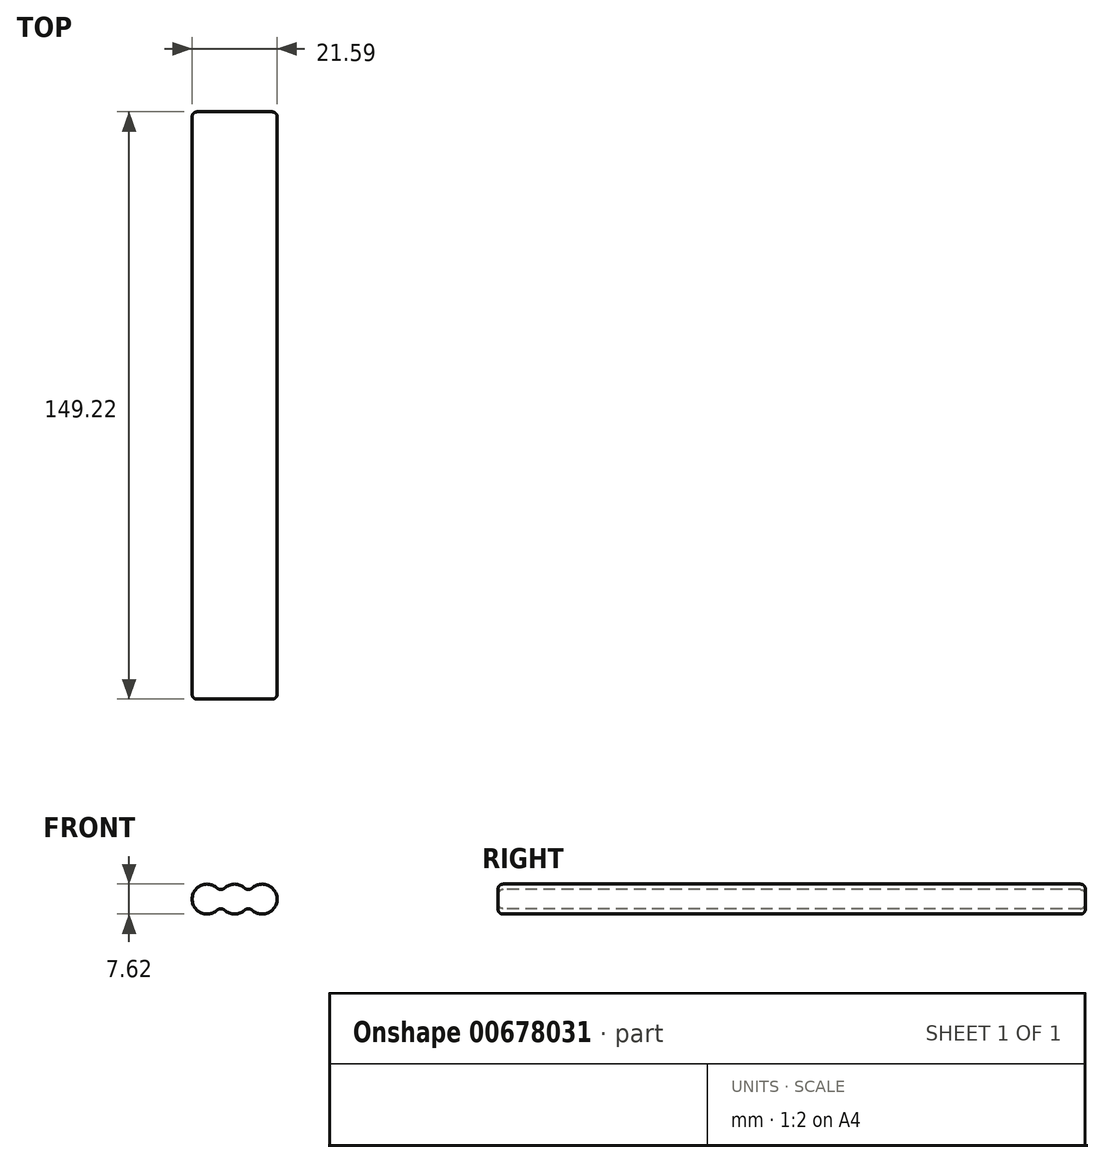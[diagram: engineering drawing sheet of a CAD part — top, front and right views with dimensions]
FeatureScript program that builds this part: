
annotation { "Feature Type Name" : "Feature", "Feature Type Description" : "" }
export const myFeature = defineFeature(function(context is Context, id is Id, definition is map)
    precondition{}
    {
        {
            var Q0;
            Q0=qCreatedBy(makeId("Front.planeOp"),FACE);
            var sketch = newSketch(context, id + "F0", { "sketchPlane" : qUnion([Q0])});
            skLineSegment(sketch, "E0", {"start": v(-6.99, 0) * mm, "end": v(6.99, 0) * mm, "construction": true});
            skArc(sketch, "E1", {"start": v(3.5, 1.52) * mm, "mid": v(0, 3.8) * mm, "end": v(-3.5, 1.52) * mm});
            skArc(sketch, "E2", {"start": v(3.5, -1.52) * mm, "mid": v(10.8, 0) * mm, "end": v(3.5, 1.52) * mm});
            skArc(sketch, "E3", {"start": v(-3.5, 1.52) * mm, "mid": v(-10.8, 0) * mm, "end": v(-3.5, -1.52) * mm});
            skArc(sketch, "E4.trimOffspring", {"start": v(-3.5, -1.52) * mm, "mid": v(0, -3.8) * mm, "end": v(3.5, -1.52) * mm});
            skSolve(sketch);
        }
        {
            var Q0;
            Q0 = qSketchRegion(id + "F0", true);
            extrude(context, id + "F1", {"entities" : qUnion([Q0]), "endBound" : BoundingType.SYMMETRIC, "depth" : 149.22 * mm, "offsetDistance" : 25.4 * mm});
        }
        {
            var Q0;
            Q0=makeQuery(id+"F1.opExtrude","CAP_FACE",FACE,{"disambiguationData":[OSD([sQuery(id+"F0.wireOp",EDGE,"E1"),sQuery(id+"F0.wireOp",EDGE,"E2"),sQuery(id+"F0.wireOp",EDGE,"E3"),sQuery(id+"F0.wireOp",EDGE,"E4.trimOffspring")])],"isStart":true});
            var Q1;
            Q1=makeQuery(id+"F1.opExtrude","SWEPT_EDGE",EDGE,{"disambiguationData":[OSD([sQuery(id+"F0.wireOp",EDGE,"E1"),sQuery(id+"F0.wireOp",EDGE,"E2")])]});
            var Q2;
            Q2=makeQuery(id+"F1.opExtrude","SWEPT_EDGE",EDGE,{"disambiguationData":[OSD([sQuery(id+"F0.wireOp",EDGE,"E1"),sQuery(id+"F0.wireOp",EDGE,"E3")])]});
            var Q3;
            Q3=makeQuery(id+"F1.opExtrude","SWEPT_EDGE",EDGE,{"disambiguationData":[OSD([sQuery(id+"F0.wireOp",EDGE,"E2"),sQuery(id+"F0.wireOp",EDGE,"E4.trimOffspring")])]});
            var Q4;
            Q4=makeQuery(id+"F1.opExtrude","SWEPT_EDGE",EDGE,{"disambiguationData":[OSD([sQuery(id+"F0.wireOp",EDGE,"E3"),sQuery(id+"F0.wireOp",EDGE,"E4.trimOffspring")])]});
            var Q5;
            Q5=makeQuery(id+"F1.opExtrude","CAP_FACE",FACE,{"disambiguationData":[OSD([sQuery(id+"F0.wireOp",EDGE,"E1"),sQuery(id+"F0.wireOp",EDGE,"E2"),sQuery(id+"F0.wireOp",EDGE,"E3"),sQuery(id+"F0.wireOp",EDGE,"E4.trimOffspring")])],"isStart":false});
            fillet(context, id + "F2", {"entities" : qUnion([Q0, Q1, Q2, Q3, Q4, Q5]), "radius" : 1.27 * mm, "tangentPropagation" : true, "allowEdgeOverflow" : false});
        }
    });
